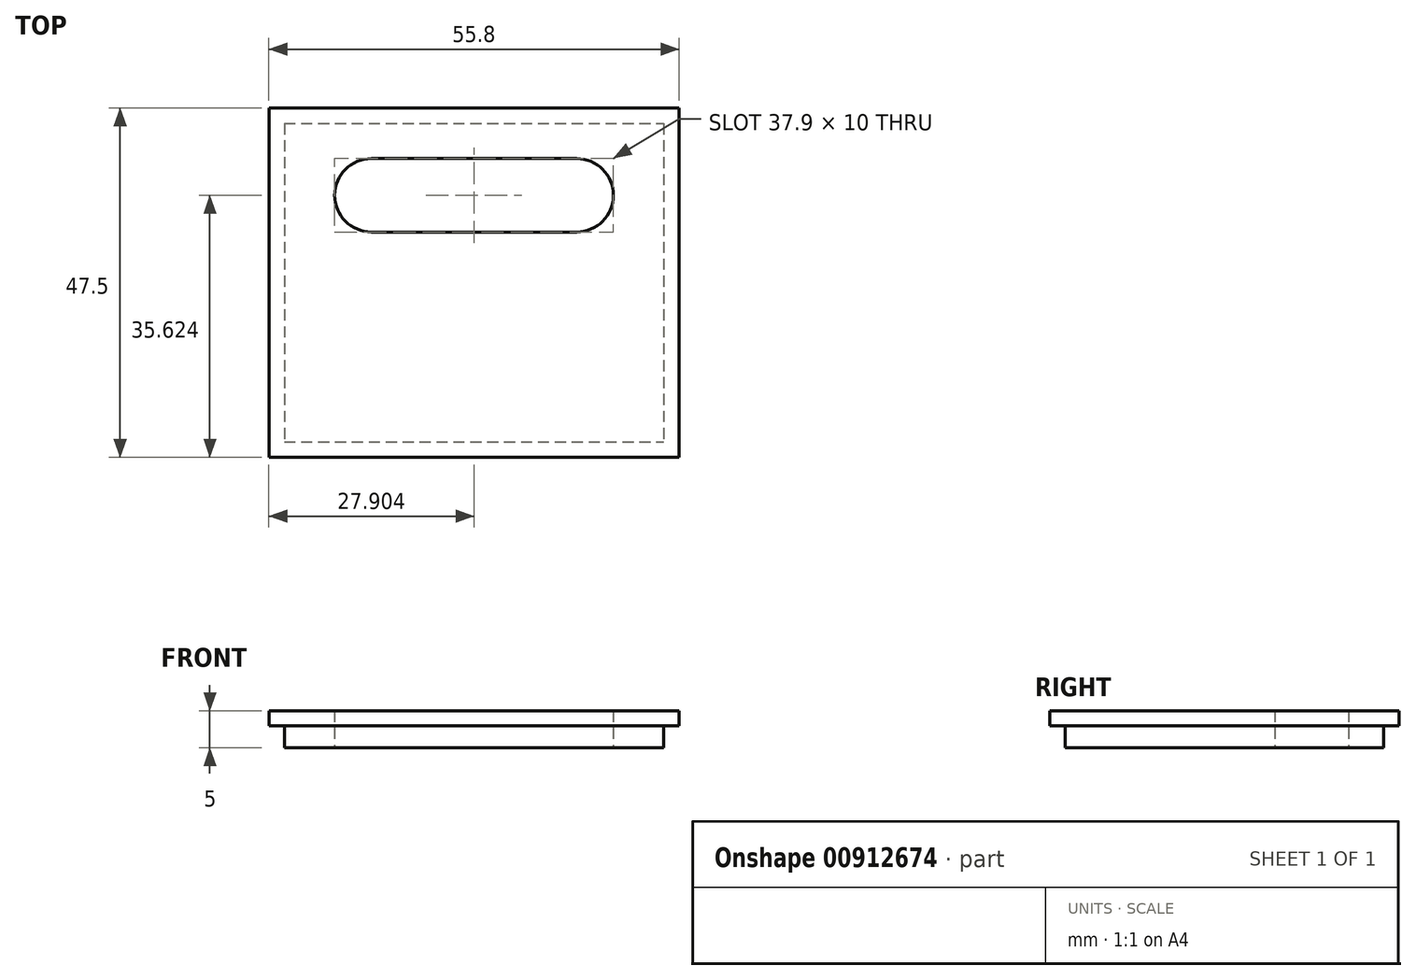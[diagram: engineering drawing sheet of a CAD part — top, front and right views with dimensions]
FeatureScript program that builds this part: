
annotation { "Feature Type Name" : "Feature", "Feature Type Description" : "" }
export const myFeature = defineFeature(function(context is Context, id is Id, definition is map)
    precondition{}
    {
        {
            var Q0;
            Q0=qCreatedBy(makeId("Top.planeOp"),FACE);
            var sketch = newSketch(context, id + "F0", { "sketchPlane" : qUnion([Q0])});
            skLineSegment(sketch, "E0.bottom", {"start": v(-64.93, 7.68) * mm, "end": v(-9.13, 7.68) * mm});
            skLineSegment(sketch, "E0.top", {"start": v(-64.93, -39.82) * mm, "end": v(-9.13, -39.82) * mm});
            skLineSegment(sketch, "E0.left", {"start": v(-64.93, 7.68) * mm, "end": v(-64.93, -39.82) * mm});
            skLineSegment(sketch, "E0.right", {"start": v(-9.13, 7.68) * mm, "end": v(-9.13, -39.82) * mm});
            skLineSegment(sketch, "E1", {"start": v(-9.13, -16.07) * mm, "end": v(-9.13, 7.68) * mm});
            skArc(sketch, "E2", {"start": v(-50.98, 0.8) * mm, "mid": v(-55.98, -4.2) * mm, "end": v(-50.98, -9.2) * mm});
            skArc(sketch, "E3", {"start": v(-23.08, -9.2) * mm, "mid": v(-18.08, -4.2) * mm, "end": v(-23.08, 0.8) * mm});
            skLineSegment(sketch, "E4.bottom", {"start": v(-23.08, -9.2) * mm, "end": v(-50.98, -9.2) * mm});
            skLineSegment(sketch, "E4.top", {"start": v(-23.08, 0.8) * mm, "end": v(-50.98, 0.8) * mm});
            skPoint(sketch, "E4.middle", {"position": v(-37.03, -4.2) * mm});
            skPoint(sketch, "E5.orphan", {"position": v(-37.03, -39.82) * mm});
            skPoint(sketch, "E6.start.orphan", {"position": v(-64.93, -16.07) * mm});
            skPoint(sketch, "E7.start.orphan", {"position": v(-37.03, 7.68) * mm});
            skPoint(sketch, "E8.start.orphan", {"position": v(-64.93, -4.2) * mm});
            skPoint(sketch, "E9.trimOffspring.end.orphan", {"position": v(-9.13, -4.2) * mm});
            skSolve(sketch);
        }
        {
            var Q0;
            Q0=makeQuery(id+"F0.imprint","IMPRINT",FACE,{"disambiguationData":[TD([[makeQuery(id+"F0.imprint","IMPRINT",EDGE,{"derivedFrom":sQuery(id+"F0.wireOp",EDGE,"E0.bottom")}),-1.0]])]});
            extrude(context, id + "F1", {"entities" : qUnion([Q0]), "depth" : 2 * mm, "offsetDistance" : 25 * mm});
        }
        {
            var Q0;
            Q0=makeQuery(id+"F1.opExtrude","CAP_FACE",FACE,{"disambiguationData":[OSD([sQuery(id+"F0.wireOp",EDGE,"E0.bottom"),sQuery(id+"F0.wireOp",EDGE,"E0.top"),sQuery(id+"F0.wireOp",EDGE,"E0.left"),sQuery(id+"F0.wireOp",EDGE,"E0.right"),sQuery(id+"F0.wireOp",EDGE,"E1"),sQuery(id+"F0.wireOp",EDGE,"E2"),sQuery(id+"F0.wireOp",EDGE,"E3"),sQuery(id+"F0.wireOp",EDGE,"E4.bottom"),sQuery(id+"F0.wireOp",EDGE,"E4.top")])],"isStart":true});
            var sketch = newSketch(context, id + "F2", { "sketchPlane" : qUnion([Q0])});
            skLineSegment(sketch, "E10.0", {"start": v(-11.23, -5.58) * mm, "end": v(-11.23, 37.72) * mm});
            skLineSegment(sketch, "E10.1", {"start": v(-62.83, -5.58) * mm, "end": v(-11.23, -5.58) * mm});
            skLineSegment(sketch, "E10.2", {"start": v(-62.83, -5.58) * mm, "end": v(-62.83, 37.72) * mm});
            skLineSegment(sketch, "E10.3", {"start": v(-62.83, 37.72) * mm, "end": v(-11.23, 37.72) * mm});
            skSolve(sketch);
        }
        {
            var Q0;
            Q0 = qSketchRegion(id + "F2", true);
            extrude(context, id + "F3", {"entities" : qUnion([Q0]), "operationType" : NewBodyOperationType.ADD, "depth" : 3 * mm, "offsetDistance" : 25 * mm});
        }
        {
            var Q0;
            Q0=makeQuery(id+"F3.opExtrude","CAP_FACE",FACE,{"disambiguationData":[OSD([sQuery(id+"F2.wireOp",EDGE,"E10.0"),sQuery(id+"F2.wireOp",EDGE,"E10.1"),sQuery(id+"F2.wireOp",EDGE,"E10.2"),sQuery(id+"F2.wireOp",EDGE,"E10.3")])],"isStart":true});
            extrude(context, id + "F4", {"entities" : qUnion([Q0]), "operationType" : NewBodyOperationType.REMOVE, "oppositeDirection" : true, "depth" : 17.9 * mm, "offsetDistance" : 25 * mm});
        }
    });
